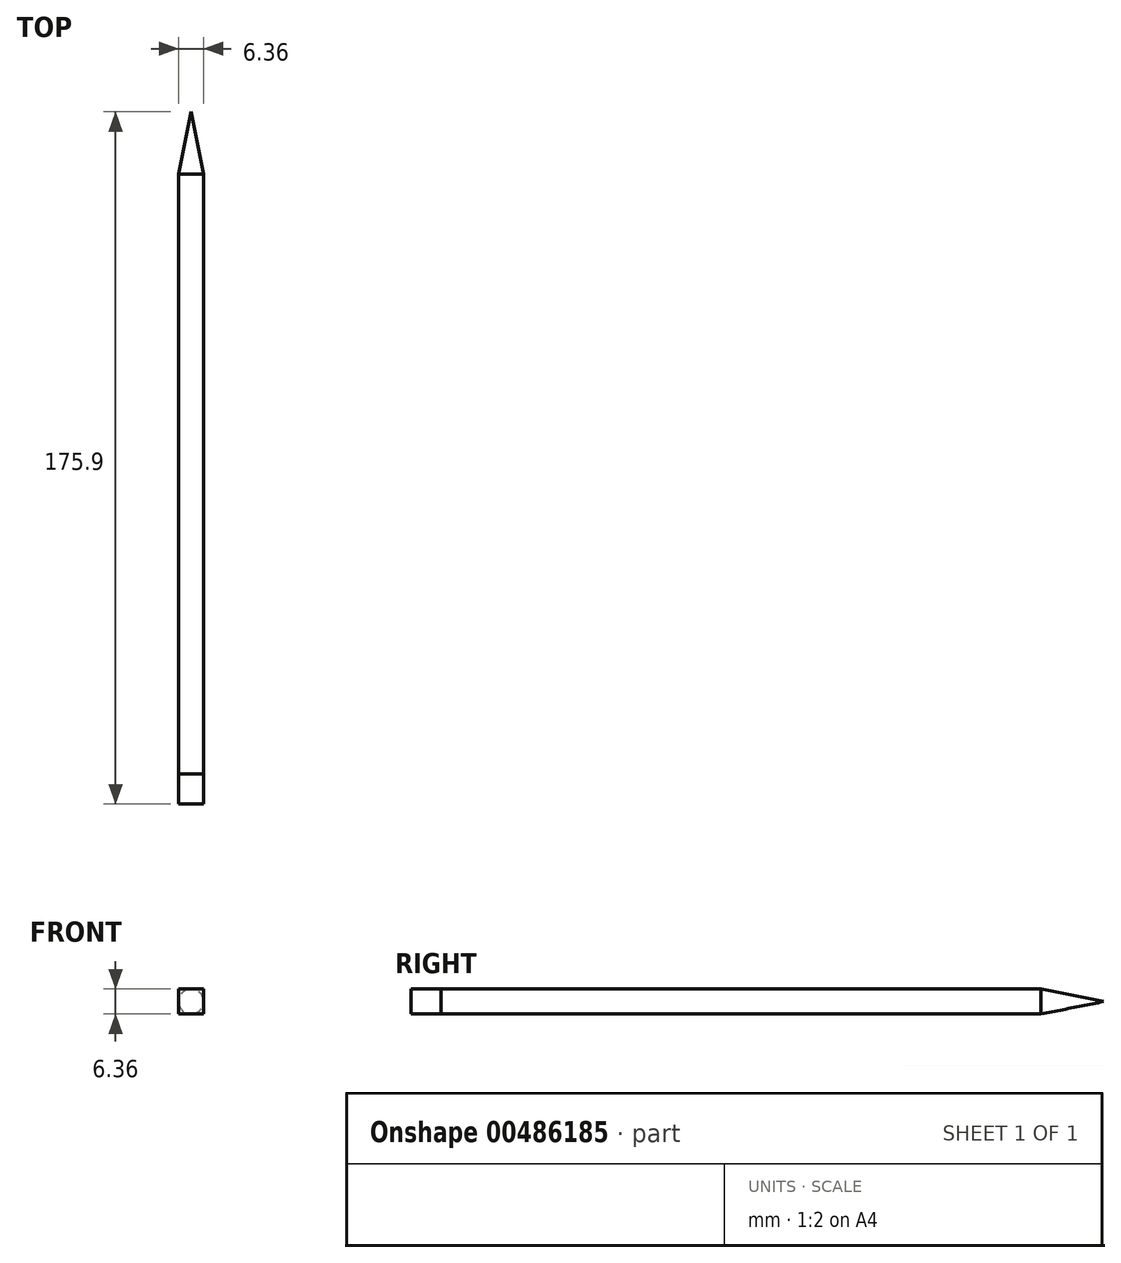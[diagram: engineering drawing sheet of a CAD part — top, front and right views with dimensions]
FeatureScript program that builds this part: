
annotation { "Feature Type Name" : "Feature", "Feature Type Description" : "" }
export const myFeature = defineFeature(function(context is Context, id is Id, definition is map)
    precondition{}
    {
        {
            var Q0;
            Q0=qCreatedBy(makeId("Front.planeOp"),FACE);
            var sketch = newSketch(context, id + "F0", { "sketchPlane" : qUnion([Q0])});
            skCircle(sketch, "E0", {"center": v(0, 0) * mm, "radius": 3.18 * mm});
            skSolve(sketch);
        }
        {
            var Q0;
            Q0=makeQuery(id+"F0.imprint","IMPRINT",FACE,{"disambiguationData":[TD([[makeQuery(id+"F0.imprint","IMPRINT",EDGE,{"derivedFrom":sQuery(id+"F0.wireOp",EDGE,"E0")}),1.0]])]});
            extrude(context, id + "F1", {"entities" : qUnion([Q0]), "depth" : 152.4 * mm, "symmetric" : true});
        }
        {
            var Q0;
            Q0=qCreatedBy(makeId("Top.planeOp"),FACE);
            var sketch = newSketch(context, id + "F2", { "sketchPlane" : qUnion([Q0])});
            skLineSegment(sketch, "E1", {"start": v(0, 0) * mm, "end": v(0, 76.2) * mm});
            skLineSegment(sketch, "E2", {"start": v(0, 76.2) * mm, "end": v(3.18, 76.2) * mm});
            skLineSegment(sketch, "E3", {"start": v(3.18, 76.2) * mm, "end": v(0, 92.08) * mm});
            skLineSegment(sketch, "E4", {"start": v(0, 92.08) * mm, "end": v(0, 76.2) * mm});
            skSolve(sketch);
        }
        {
            var Q0;
            Q0=makeQuery(id+"F2.imprint","IMPRINT",FACE,{"disambiguationData":[TD([[makeQuery(id+"F2.imprint","IMPRINT",EDGE,{"derivedFrom":sQuery(id+"F2.wireOp",EDGE,"E2")}),1.0]])]});
            var Q1;
            Q1=sQuery(id+"F2.wireOp",EDGE,"E4");
            revolve(context, id + "F3", {"operationType" : NewBodyOperationType.ADD, "entities" : qUnion([Q0]), "axis" : qUnion([Q1]), "revolveType" : RevolveType.FULL});
        }
        {
            var Q0;
            Q0=qCreatedBy(makeId("Top.planeOp"),FACE);
            var sketch = newSketch(context, id + "F4", { "sketchPlane" : qUnion([Q0])});
            skLineSegment(sketch, "E5", {"start": v(0, 0) * mm, "end": v(0, -76.2) * mm});
            skLineSegment(sketch, "E6", {"start": v(0, -76.2) * mm, "end": v(3.18, -76.2) * mm});
            skLineSegment(sketch, "E7", {"start": v(3.18, -76.2) * mm, "end": v(3.18, -83.82) * mm});
            skLineSegment(sketch, "E8", {"start": v(3.18, -83.82) * mm, "end": v(-3.17, -83.82) * mm});
            skLineSegment(sketch, "E9", {"start": v(-3.17, -83.82) * mm, "end": v(-3.17, -76.2) * mm});
            skLineSegment(sketch, "E10", {"start": v(-3.17, -76.2) * mm, "end": v(0, -76.2) * mm});
            skSolve(sketch);
        }
        {
            var Q0;
            Q0=makeQuery(id+"F4.imprint","IMPRINT",FACE,{"disambiguationData":[TD([[makeQuery(id+"F4.imprint","IMPRINT",EDGE,{"derivedFrom":sQuery(id+"F4.wireOp",EDGE,"E6")}),-1.0]])]});
            extrude(context, id + "F5", {"entities" : qUnion([Q0]), "operationType" : NewBodyOperationType.ADD, "depth" : 6.35 * mm, "symmetric" : true});
        }
    });
